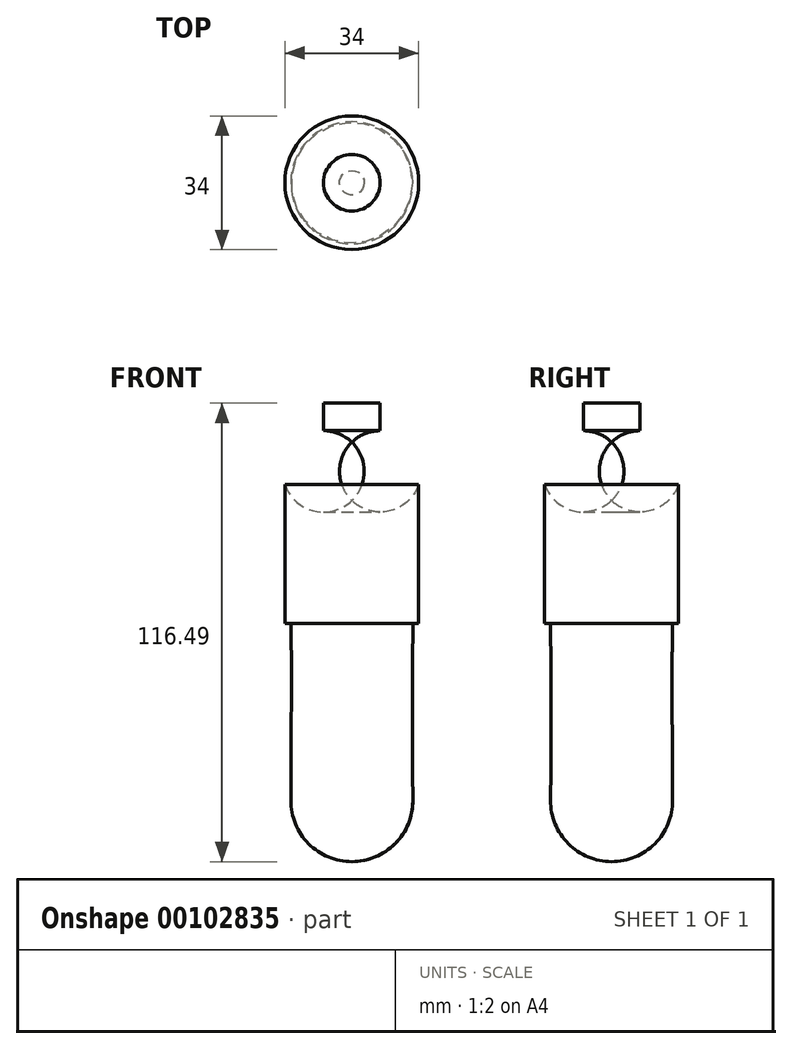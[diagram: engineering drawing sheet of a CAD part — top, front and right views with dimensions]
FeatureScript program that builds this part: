
annotation { "Feature Type Name" : "Feature", "Feature Type Description" : "" }
export const myFeature = defineFeature(function(context is Context, id is Id, definition is map)
    precondition{}
    {
        {
            var Q0;
            Q0=qCreatedBy(makeId("Front.planeOp"),FACE);
            var sketch = newSketch(context, id + "F0", { "sketchPlane" : qUnion([Q0])});
            skLineSegment(sketch, "E0", {"start": v(0, 0) * mm, "end": v(0, 56) * mm});
            skLineSegment(sketch, "E1", {"start": v(0, 0) * mm, "end": v(17, 0) * mm});
            skLineSegment(sketch, "E2", {"start": v(0, 56) * mm, "end": v(7.2, 56) * mm});
            skLineSegment(sketch, "E3", {"start": v(7.2, 56) * mm, "end": v(7.2, 49) * mm});
            skArc(sketch, "E4", {"start": v(17, 35.4) * mm, "mid": v(15.58, 44.7) * mm, "end": v(7.2, 49) * mm});
            skLineSegment(sketch, "E5", {"start": v(17, 35.4) * mm, "end": v(17, 0) * mm});
            skLineSegment(sketch, "E6", {"start": v(0, 0) * mm, "end": v(0, -60.49) * mm});
            skArc(sketch, "E7", {"start": v(0, -60.49) * mm, "mid": v(11, -55.92) * mm, "end": v(15.5, -44.9) * mm});
            skFitSpline(sketch, "E8", {"points": [v(15.5, 0) * mm, v(15.5, -44.9) * mm], "startDerivative": vector(0, -52.42) * mm, "endDerivative": vector(0.95, -172.3) * mm});
            skSolve(sketch);
        }
        {
            var Q0;
            {var subQ3=sQuery(id+"F0.wireOp",EDGE,"E0");Q0=makeQuery(id+"F0.imprint","IMPRINT",FACE,{"disambiguationData":[TD([[makeQuery(id+"F0.imprint","IMPRINT",EDGE,{"derivedFrom":subQ3}),-1.0]])]});}
            var Q1;
            Q1=sQuery(id+"F0.wireOp",EDGE,"E0");
            revolve(context, id + "F1", {"entities" : qUnion([Q0]), "axis" : qUnion([Q1]), "revolveType" : RevolveType.FULL});
        }
        {
            var Q0;
            {var subQ0=sQuery(id+"F0.wireOp",EDGE,"E6");Q0=makeQuery(id+"F0.imprint","IMPRINT",FACE,{"disambiguationData":[TD([[makeQuery(id+"F0.imprint","IMPRINT",EDGE,{"derivedFrom":subQ0}),1.0]])]});}
            var Q1;
            Q1=sQuery(id+"F0.wireOp",EDGE,"E6");
            revolve(context, id + "F2", {"entities" : qUnion([Q0]), "axis" : qUnion([Q1]), "revolveType" : RevolveType.FULL});
        }
    });
